# Revit family: P200921MX-055c_MMV5227JZ
name_source: partatom
category: Specialty Equipment
units: mm (PartAtom-declared; Revit-internal decimal feet)

## family parameters
Always vertical = No
Cut with Voids When Loaded = No
Enable Cutting in Views = No
Maintain Annotation Orientation = No
Part Type = Normal
Room Calculation Point = No
Round Connector Dimension = Use Diameter
Shared = No
Work Plane-Based = No

## types (1)
- MMV5227JZ
    Amps = 0 A
    Back Panel Material = ARCAT - Metal - Aluminum
    Body Material = ARCAT - Metal - Steel - Black
    Clearance Material = ARCAT - Clearance
    Default Elevation = 0"
    Depth = 17 9/16"
    Description = Over-the-Range Microwave with Dual Crisp feature - 1.9 cu. ft.
    Display Material = ARCAT - Glass - Tempered - Black - Dark
    Display Panel Material = ARCAT - Glass - Tempered - Black
    Door Material = ARCAT - Metal - Steel - Stainless
    Family Name = Cooking
    Feature 1 = Dual Crisp feature with crisping tray
    Feature 2 = Fingerprint resistant stainless steel
    Feature 3 = Brown function
    Glass Material = ARCAT - Glass - Tempered - Black - Light
    Handle Material = ARCAT - Metal - Steel -Gray - Light
    Height = 17 1/8"
    Installation-Fabrication = https://www.whirlpool.com
    Leg Material = ARCAT - Metal - Plastic - Black
    Manufacturer = Maytag
    Model = MMV5227JZ
    Voltage = 0 V
    Width = 29 15/16"

## geometry (parser evidence)
native form markers: Sweep x7
no freeform markers — native parametric forms only
